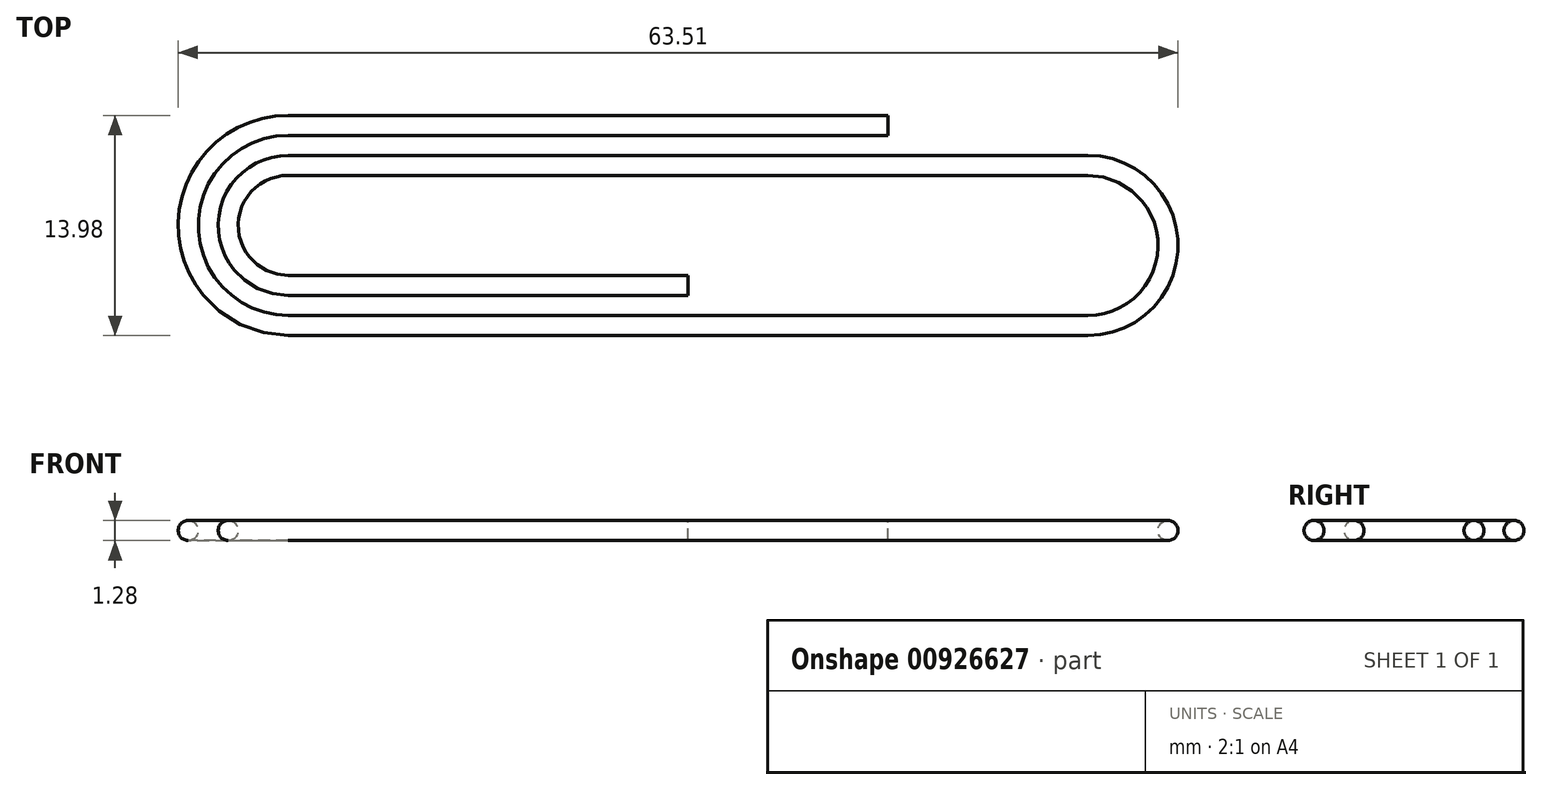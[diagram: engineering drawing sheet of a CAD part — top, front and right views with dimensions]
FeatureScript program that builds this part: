
annotation { "Feature Type Name" : "Feature", "Feature Type Description" : "" }
export const myFeature = defineFeature(function(context is Context, id is Id, definition is map)
    precondition{}
    {
        {
            var Q0;
            Q0=qCreatedBy(makeId("Top.planeOp"),FACE);
            var sketch = newSketch(context, id + "F0", { "sketchPlane" : qUnion([Q0])});
            skLineSegment(sketch, "E0", {"start": v(12.7, 10.16) * mm, "end": v(-25.4, 10.16) * mm});
            skArc(sketch, "E1", {"start": v(-25.4, 10.16) * mm, "mid": v(-31.75, 3.8) * mm, "end": v(-25.4, -2.54) * mm});
            skLineSegment(sketch, "E2", {"start": v(-25.4, -2.54) * mm, "end": v(25.4, -2.54) * mm});
            skArc(sketch, "E3", {"start": v(25.4, -2.54) * mm, "mid": v(30.48, 2.54) * mm, "end": v(25.4, 7.62) * mm});
            skLineSegment(sketch, "E4", {"start": v(25.4, 7.62) * mm, "end": v(-25.4, 7.62) * mm});
            skArc(sketch, "E5", {"start": v(-25.4, 7.62) * mm, "mid": v(-29.21, 3.81) * mm, "end": v(-25.4, 0) * mm});
            skLineSegment(sketch, "E6", {"start": v(-25.4, 0) * mm, "end": v(0, 0) * mm});
            skSolve(sketch);
        }
        {
            var Q0;
            Q0=qCreatedBy(makeId("Right.planeOp"),FACE);
            var sketch = newSketch(context, id + "F1", { "sketchPlane" : qUnion([Q0])});
            skCircle(sketch, "E7", {"center": v(0, 0) * mm, "radius": 0.64 * mm});
            skSolve(sketch);
        }
        {
            var Q0;
            Q0=makeQuery(id+"F1.imprint","IMPRINT",FACE,{"disambiguationData":[TD([[makeQuery(id+"F1.imprint","IMPRINT",EDGE,{"derivedFrom":sQuery(id+"F1.wireOp",EDGE,"E7")}),1.0]])]});
            var Q1;
            Q1 = qConstructionFilter(qBodyType(qCreatedBy(id + "F0" ,EDGE), BodyType.WIRE), ConstructionObject.NO);
            sweep(context, id + "F2", {"profiles" : qUnion([Q0]), "path" : qUnion([Q1])});
        }
    });
